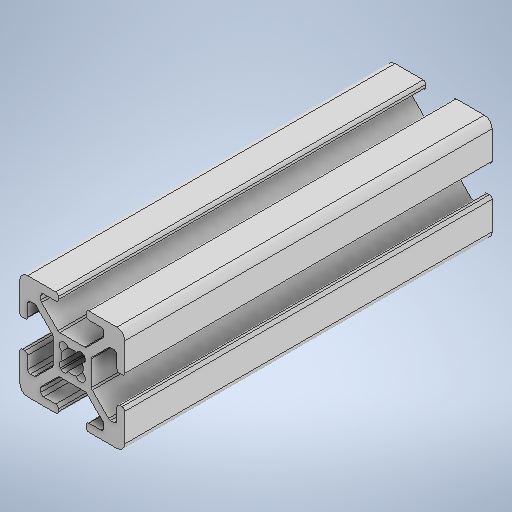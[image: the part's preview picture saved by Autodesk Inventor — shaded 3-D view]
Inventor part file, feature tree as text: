
AUTODESK INVENTOR PART (.ipt)
format: ipt  version: 2025 (Build 290162000, 162)  size: 357,888 bytes
history: native  units: mm
features: extrude x1, sketch x1
ambient origin geometry x8: Origin, YZ Plane, XZ Plane, XY Plane, X Axis, Y Axis, Z Axis, Center Point
bodies: Solid1 (feature_tree)
feature tree (2):
  extrude  "Extrusion1"  Depth=70.0mm
  sketch  "Sketch1"  dims[d0=70.0mm d1=0.0mm d2=1.0mm d3=1.0mm d4=1.0mm d5=0.15mm d6=0.25mm d7=0.375mm d8=14.3117mm d9=0.75mm d10=20.594885mm d11=0.0625mm d12=0.75mm d13=0.375mm]
